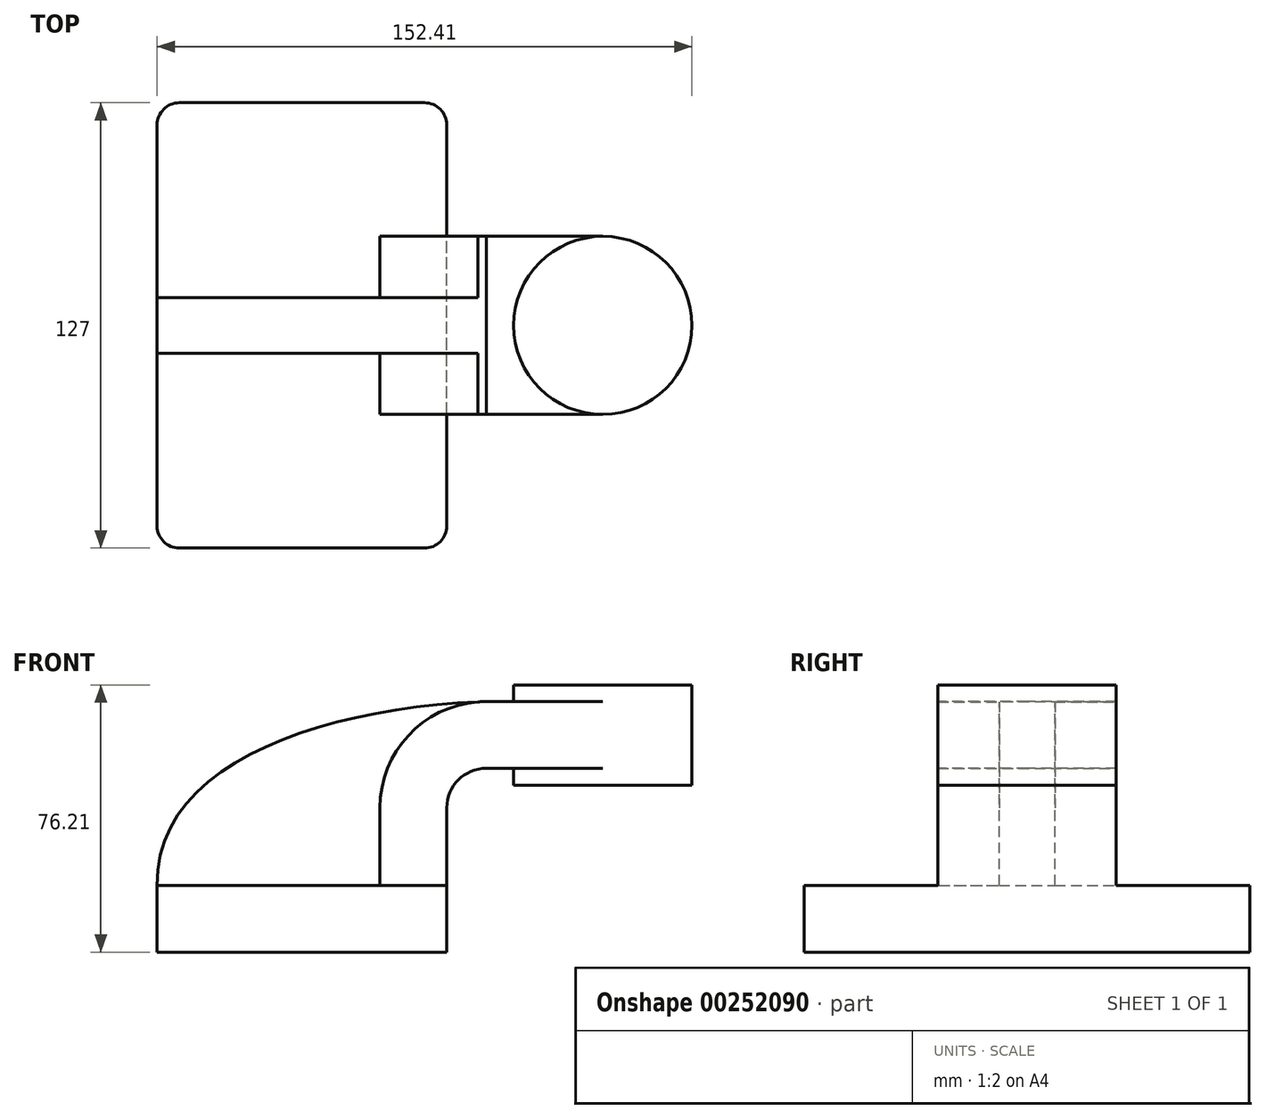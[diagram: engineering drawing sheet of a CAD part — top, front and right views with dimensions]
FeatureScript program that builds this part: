
annotation { "Feature Type Name" : "Feature", "Feature Type Description" : "" }
export const myFeature = defineFeature(function(context is Context, id is Id, definition is map)
    precondition{}
    {
        {
            var Q0;
            Q0=qCreatedBy(makeId("Front.planeOp"),FACE);
            var sketch = newSketch(context, id + "F0", { "sketchPlane" : qUnion([Q0])});
            skLineSegment(sketch, "E0.bottom", {"start": v(41.27, 9.53) * mm, "end": v(-41.28, 9.53) * mm});
            skLineSegment(sketch, "E0.top", {"start": v(41.28, -9.52) * mm, "end": v(-41.28, -9.52) * mm});
            skLineSegment(sketch, "E0.left", {"start": v(41.28, 9.53) * mm, "end": v(41.28, -9.52) * mm});
            skLineSegment(sketch, "E0.right", {"start": v(-41.28, 9.53) * mm, "end": v(-41.28, -9.52) * mm});
            skPoint(sketch, "E0.middle", {"position": v(0, 0) * mm});
            skLineSegment(sketch, "E1", {"start": v(41.27, 9.53) * mm, "end": v(41.27, 31.63) * mm});
            skLineSegment(sketch, "E2.top", {"start": v(90.44, 88.01) * mm, "end": v(90.44, 88.01) * mm});
            skLineSegment(sketch, "E3.bottom", {"start": v(111.12, 38.1) * mm, "end": v(60.33, 38.1) * mm});
            skLineSegment(sketch, "E3.top", {"start": v(111.12, 66.68) * mm, "end": v(60.33, 66.68) * mm});
            skLineSegment(sketch, "E3.left", {"start": v(111.12, 38.1) * mm, "end": v(111.12, 66.68) * mm});
            skLineSegment(sketch, "E3.right", {"start": v(60.33, 38.1) * mm, "end": v(60.33, 66.68) * mm});
            skPoint(sketch, "E3.middle", {"position": v(85.72, 52.39) * mm});
            skArc(sketch, "E4", {"start": v(41.28, 31.63) * mm, "mid": v(44.57, 39.58) * mm, "end": v(52.52, 42.88) * mm});
            skLineSegment(sketch, "E5", {"start": v(52.52, 42.88) * mm, "end": v(85.72, 42.88) * mm});
            skPoint(sketch, "E5.endSnap0", {"position": v(85.72, 38.1) * mm});
            skLineSegment(sketch, "E6.0", {"start": v(52.52, 61.93) * mm, "end": v(85.72, 61.93) * mm});
            skArc(sketch, "E6.1", {"start": v(22.23, 31.63) * mm, "mid": v(31.1, 53.05) * mm, "end": v(52.52, 61.93) * mm});
            skLineSegment(sketch, "E6.2", {"start": v(22.22, 9.53) * mm, "end": v(22.22, 31.63) * mm});
            skLineSegment(sketch, "E7", {"start": v(85.72, 38.1) * mm, "end": v(85.72, 66.68) * mm});
            skFitSpline(sketch, "E8", {"points": [v(-41.28, 9.52) * mm, v(52.52, 61.93) * mm], "startDerivative": vector(-1.8, 105.82) * mm, "endDerivative": vector(137.1, 4.63) * mm});
            skSolve(sketch);
        }
        {
            var Q0;
            Q0=makeQuery(id+"F0.imprint","IMPRINT",FACE,{"disambiguationData":[TD([[makeQuery(id+"F0.imprint","IMPRINT",EDGE,{"derivedFrom":sQuery(id+"F0.wireOp",EDGE,"E0.top")}),-1.0]])]});
            extrude(context, id + "F1", {"entities" : qUnion([Q0]), "endBound" : BoundingType.SYMMETRIC, "depth" : 127 * mm});
        }
        {
            var Q0;
            {var subQ6=sQuery(id+"F0.wireOp",EDGE,"E1");Q0=makeQuery(id+"F0.imprint","IMPRINT",FACE,{"disambiguationData":[TD([[makeQuery(id+"F0.imprint","IMPRINT",EDGE,{"derivedFrom":subQ6}),1.0]])]});}
            var Q1;
            {var subQ0=sQuery(id+"F0.wireOp",EDGE,"E5");var subQ1=sQuery(id+"F0.wireOp",EDGE,"E3.right");var subQ2=makeQuery(id+"F0.imprint","INTERSECT",VERTEX,{"derivedFrom":[subQ1,subQ0]});Q1=makeQuery(id+"F0.imprint","IMPRINT",FACE,{"disambiguationData":[TD([[makeQuery(id+"F0.imprint","IMPRINT",EDGE,{"disambiguationData":[TD([[subQ2,-1.0]])],"derivedFrom":subQ1}),-1.0]])]});}
            extrude(context, id + "F2", {"entities" : qUnion([Q0, Q1]), "operationType" : NewBodyOperationType.ADD, "endBound" : BoundingType.SYMMETRIC, "depth" : 50.8 * mm});
        }
        {
            var Q0;
            {var subQ3=sQuery(id+"F0.wireOp",EDGE,"E6.2");Q0=makeQuery(id+"F0.imprint","IMPRINT",FACE,{"disambiguationData":[TD([[makeQuery(id+"F0.imprint","IMPRINT",EDGE,{"derivedFrom":subQ3}),1.0]])]});}
            extrude(context, id + "F3", {"entities" : qUnion([Q0]), "operationType" : NewBodyOperationType.ADD, "endBound" : BoundingType.SYMMETRIC, "depth" : 15.88 * mm});
        }
        {
            var Q0;
            {var subQ0=sQuery(id+"F0.wireOp",EDGE,"E3.left");Q0=makeQuery(id+"F0.imprint","IMPRINT",FACE,{"disambiguationData":[TD([[makeQuery(id+"F0.imprint","IMPRINT",EDGE,{"derivedFrom":subQ0}),1.0]])]});}
            var Q1;
            Q1=sQuery(id+"F0.wireOp",EDGE,"E7");
            revolve(context, id + "F4", {"operationType" : NewBodyOperationType.ADD, "entities" : qUnion([Q0]), "axis" : qUnion([Q1]), "revolveType" : RevolveType.FULL});
        }
        {
            var Q0;
            Q0=makeQuery(id+"F1.opExtrude","CAP_EDGE",EDGE,{"disambiguationData":[OSD([sQuery(id+"F0.wireOp",EDGE,"E0.right")])],"isStart":false});
            var Q1;
            Q1=makeQuery(id+"F1.opExtrude","CAP_EDGE",EDGE,{"disambiguationData":[OSD([sQuery(id+"F0.wireOp",EDGE,"E0.left")])],"isStart":false});
            var Q2;
            Q2=makeQuery(id+"F1.opExtrude","CAP_EDGE",EDGE,{"disambiguationData":[OSD([sQuery(id+"F0.wireOp",EDGE,"E0.left")])],"isStart":true});
            var Q3;
            Q3=makeQuery(id+"F1.opExtrude","CAP_EDGE",EDGE,{"disambiguationData":[OSD([sQuery(id+"F0.wireOp",EDGE,"E0.right")])],"isStart":true});
            fillet(context, id + "F5", {"entities" : qUnion([Q0, Q1, Q2, Q3]), "radius" : 6.35 * mm, "tangentPropagation" : true, "allowEdgeOverflow" : false});
        }
    });
